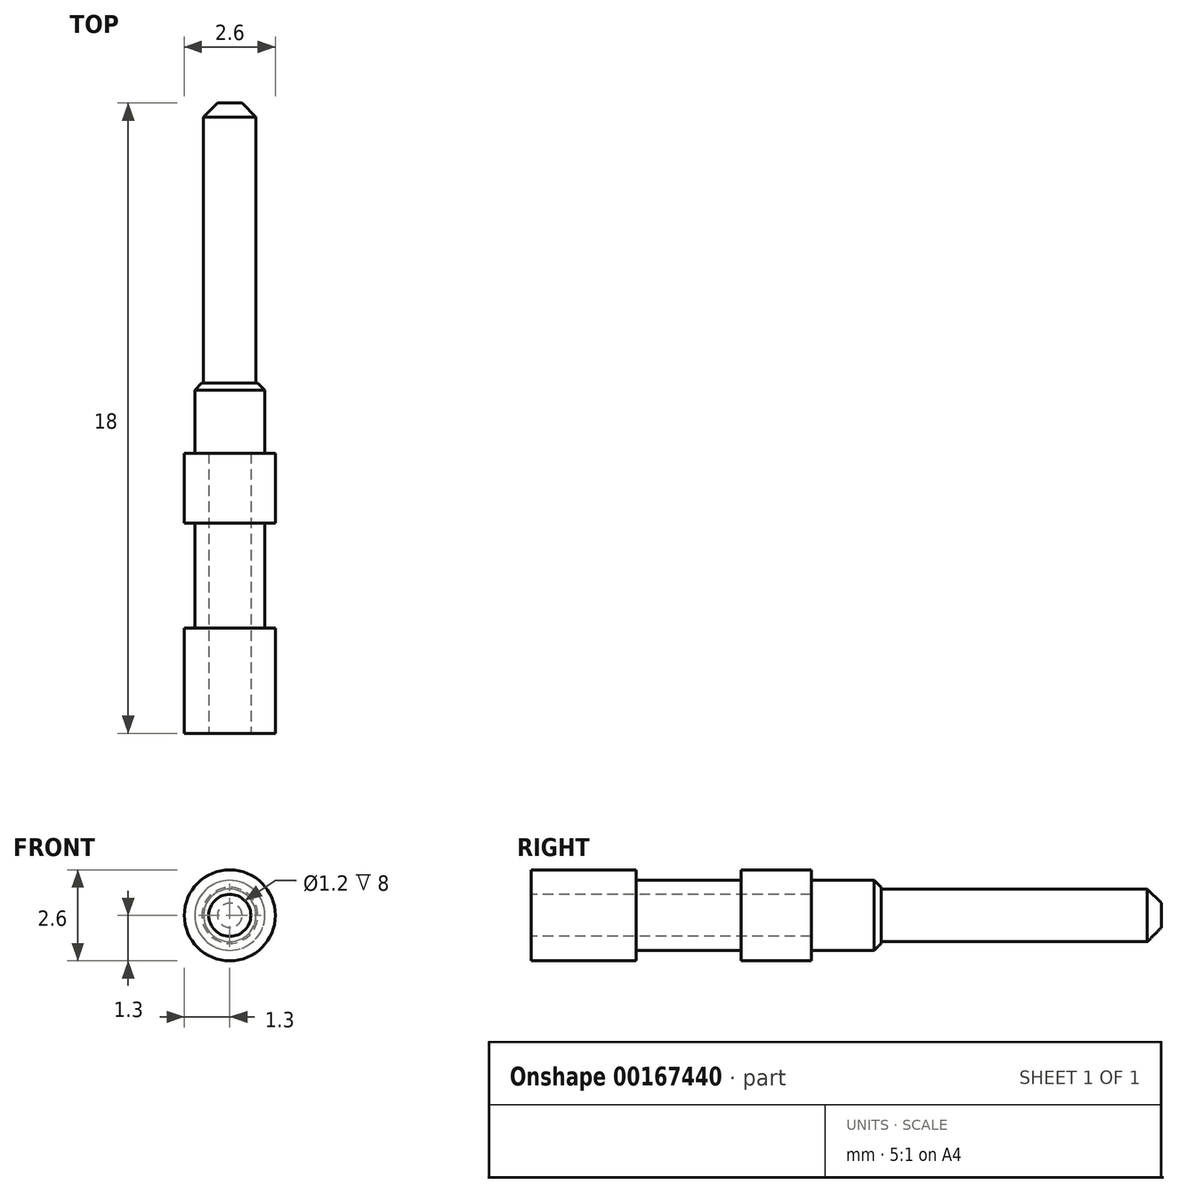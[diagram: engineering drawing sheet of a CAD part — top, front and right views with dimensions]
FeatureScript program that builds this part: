
annotation { "Feature Type Name" : "Feature", "Feature Type Description" : "" }
export const myFeature = defineFeature(function(context is Context, id is Id, definition is map)
    precondition{}
    {
        {
            var Q0;
            Q0=qCreatedBy(makeId("Right.planeOp"),FACE);
            var sketch = newSketch(context, id + "F0", { "sketchPlane" : qUnion([Q0])});
            skLineSegment(sketch, "E0", {"start": v(0, 0) * mm, "end": v(0, 1.3) * mm});
            skLineSegment(sketch, "E1", {"start": v(0, 1.3) * mm, "end": v(3, 1.3) * mm});
            skLineSegment(sketch, "E2", {"start": v(3, 1.3) * mm, "end": v(3, 1) * mm});
            skLineSegment(sketch, "E3", {"start": v(3, 1) * mm, "end": v(6, 1) * mm});
            skLineSegment(sketch, "E4", {"start": v(6, 1) * mm, "end": v(6, 1.3) * mm});
            skLineSegment(sketch, "E5", {"start": v(6, 1.3) * mm, "end": v(8, 1.3) * mm});
            skLineSegment(sketch, "E6", {"start": v(8, 1.3) * mm, "end": v(8, 1) * mm});
            skLineSegment(sketch, "E7", {"start": v(8, 1) * mm, "end": v(10, 1) * mm});
            skLineSegment(sketch, "E8", {"start": v(10, 1) * mm, "end": v(10, 0.75) * mm});
            skLineSegment(sketch, "E9", {"start": v(10, 0.75) * mm, "end": v(18, 0.75) * mm});
            skLineSegment(sketch, "E10", {"start": v(18, 0.75) * mm, "end": v(18, 0) * mm});
            skLineSegment(sketch, "E11", {"start": v(18, 0) * mm, "end": v(0, 0) * mm});
            skSolve(sketch);
        }
        {
            var Q0;
            Q0=makeQuery(id+"F0.imprint","IMPRINT",FACE,{"disambiguationData":[TD([[makeQuery(id+"F0.imprint","IMPRINT",EDGE,{"derivedFrom":sQuery(id+"F0.wireOp",EDGE,"E0")}),-1.0]])]});
            var Q1;
            Q1=sQuery(id+"F0.wireOp",EDGE,"E11");
            revolve(context, id + "F1", {"entities" : qUnion([Q0]), "axis" : qUnion([Q1]), "revolveType" : RevolveType.FULL});
        }
        {
            var Q0;
            Q0=makeQuery(id+"F1.opRevolve","SWEPT_EDGE",EDGE,{"disambiguationData":[OSD([sQuery(id+"F0.wireOp",EDGE,"E9"),sQuery(id+"F0.wireOp",EDGE,"E10")])]});
            chamfer(context, id + "F2", {"entities" : qUnion([Q0]), "width" : .4 * mm, "tangentPropagation" : true});
        }
        {
            var Q0;
            Q0=makeQuery(id+"F1.opRevolve","SWEPT_EDGE",EDGE,{"disambiguationData":[OSD([sQuery(id+"F0.wireOp",EDGE,"E7"),sQuery(id+"F0.wireOp",EDGE,"E8")])]});
            chamfer(context, id + "F3", {"entities" : qUnion([Q0]), "width" : .2 * mm, "tangentPropagation" : true});
        }
        {
            var Q0;
            Q0=makeQuery(id+"F1.opRevolve","SWEPT_FACE",FACE,{"disambiguationData":[OSD([sQuery(id+"F0.wireOp",EDGE,"E0")])]});
            var sketch = newSketch(context, id + "F4", { "sketchPlane" : qUnion([Q0])});
            skCircle(sketch, "E12", {"center": v(0, 0) * mm, "radius": 0.6 * mm});
            skSolve(sketch);
        }
        {
            var Q0;
            Q0=makeQuery(id+"F4.imprint","IMPRINT",FACE,{"disambiguationData":[TD([[makeQuery(id+"F4.imprint","IMPRINT",EDGE,{"derivedFrom":sQuery(id+"F4.wireOp",EDGE,"E12")}),1.0]])]});
            extrude(context, id + "F5", {"entities" : qUnion([Q0]), "operationType" : NewBodyOperationType.REMOVE, "oppositeDirection" : true, "depth" : 8 * mm});
        }
    });
